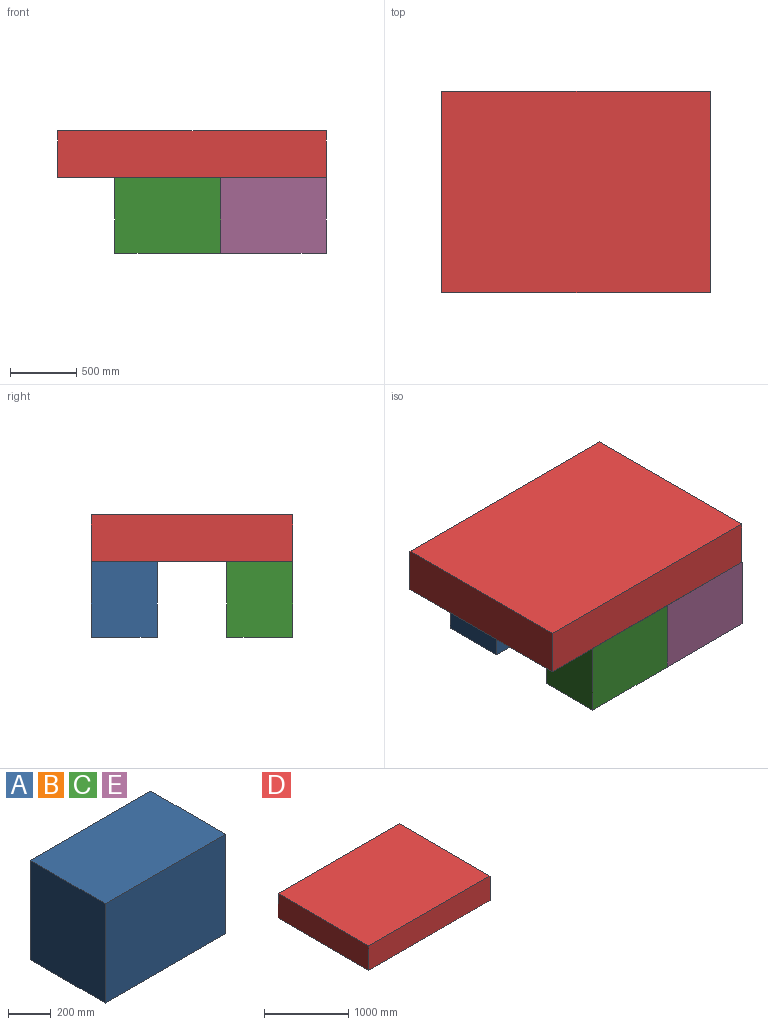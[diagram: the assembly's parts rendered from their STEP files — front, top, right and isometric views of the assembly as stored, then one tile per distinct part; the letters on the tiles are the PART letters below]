
ASSEMBLY  parts=5 mates=8
PART A: 6 faces, bbox 800.1x498.5x571.5 mm
  f0: plane 571.5x498.48mm, normal (1,0,0), area 284878.5mm2, adj f1,f3,f4,f5
  f1: plane 800.1x571.5mm, normal (0,1,0), area 457257.1mm2, adj f0,f2,f4,f5
  f2: plane 571.5x498.48mm, normal (-1,0,0), area 284878.5mm2, adj f1,f3,f4,f5
  f3: plane 800.1x571.5mm, normal (0,-1,0), area 457257.1mm2, adj f0,f2,f4,f5
  f4: plane 800.1x498.48mm, normal (0,0,1), area 398829.8mm2, adj f0,f1,f2,f3
  f5: plane 800.1x498.48mm, normal (0,0,-1), area 398829.8mm2, adj f0,f1,f2,f3
PART B: same geometry as A
PART C: same geometry as A
PART D: 6 faces, bbox 2032x1524x355.6 mm
  f0: plane 1524x355.6mm, normal (1,0,0), area 541934.4mm2, adj f1,f3,f4,f5
  f1: plane 2032x355.6mm, normal (0,1,0), area 722579.2mm2, adj f0,f2,f4,f5
  f2: plane 1524x355.6mm, normal (-1,0,0), area 541934.4mm2, adj f1,f3,f4,f5
  f3: plane 2032x355.6mm, normal (0,-1,0), area 722579.2mm2, adj f0,f2,f4,f5
  f4: plane 2032x1524mm, normal (0,0,-1), area 3096768mm2, adj f0,f1,f2,f3
  f5: plane 2032x1524mm, normal (0,0,1), area 3096768mm2, adj f0,f1,f2,f3
PART E: same geometry as A
PLACE A t=(-184.15,512.76,-927.1)mm
PLACE B rot(axis=(0,0,1),0deg) t=(615.95,512.76,-927.1)mm
PLACE C t=(-184.15,-512.76,-927.1)mm
PLACE D at identity fixed
PLACE E t=(615.95,-512.76,-927.1)mm
MATE planar B.f0 <-> D.f0  axis (1,0,0) through (1016,512.76,-641.35)mm
MATE planar B.f1 <-> D.f1  axis (0,1,0) through (615.95,762,-641.35)mm
MATE planar E.f3 <-> D.f3  axis (0,-1,0) through (615.95,-762,-641.35)mm
MATE planar B.f4 <-> D.f4  axis (0,0,1) through (615.95,512.76,-355.6)mm
MATE planar E.f0 <-> D.f0  axis (1,0,0) through (1016,-512.76,-641.35)mm
MATE fastened B.f2 <-> A.f0  axis (-1,0,0) through (215.9,762,-355.6)mm
MATE planar C.f4 <-> D.f4  axis (0,0,1) through (-184.15,-512.76,-355.6)mm
MATE fastened E.f2 <-> C.f0  axis (-1,0,0) through (215.9,-762,-355.6)mm
